# Revit family: Ghent - Spirit Series - Display Collection
name_source: partatom
category: Furniture
units: mm (PartAtom-declared; Revit-internal decimal feet)

## family parameters
Always vertical = Yes
Cut with Voids When Loaded = No
OmniClass Number = 23.40.20.00
OmniClass Title = General Furniture and Specialties
Room Calculation Point = No
Shared = No
Work Plane-Based = No

## types (6) — shared parameters
12 Shelves = No
Depth = 1' - 4"
Height = 6' - 0"
Manufacturer = Ghent
Number of Shelves = 2
Shelf Base Height = 1' - 0 3/8"
Shelf Depth = 1' - 2"
Side A Bottom = 1' - 9 1/2"
Side A Top = 1' - 0"
Side B Bottom = 0' - 9 1/2"
Side B Top = 2' - 1"
URL = https://ghent.com

## per-type parameters (varying)
| type | Case Height Interior | Cornice | Frame Height | Model | Shelf Unit Width | Width |
| Unlighted Floor Case - 72"H x 48"W x 16"D | 4' - 11 5/8" | No | 6' - 0" | 374XX-XX-XX | 1' - 11 3/4" | 4' - 0" |
| Lighted Floor Case - 72"H x 48"W x 16"D | 4' - 3 5/8" | Yes | 5' - 4" | 3714XX-XX-XX | 1' - 11 3/4" | 4' - 0" |
| Lighted Floor Case - 72"H x 60"W x 16"D | 4' - 3 5/8" | Yes | 5' - 4" | 375XX-XX-XX | 2' - 5 3/4" | 5' - 0" |
| Unlighted Floor Case - 72"H x 60"W x 16"D | 4' - 11 5/8" | No | 6' - 0" | 3175XX-XX-XX | 2' - 5 3/4" | 5' - 0" |
| Lighted Floor Case - 72"H x 72"W x 16"D | 4' - 3 5/8" | Yes | 5' - 4" | 376XX-XX-XX | 2' - 11 3/4" | 6' - 0" |
| Unlighted Floor Case - 72"H x 72"W x 16"D | 4' - 11 5/8" | No | 6' - 0" | 3176XX-XX-XX | 2' - 11 3/4" | 6' - 0" |

## geometry (parser evidence)
native form markers: Sweep x17
no freeform markers — native parametric forms only
